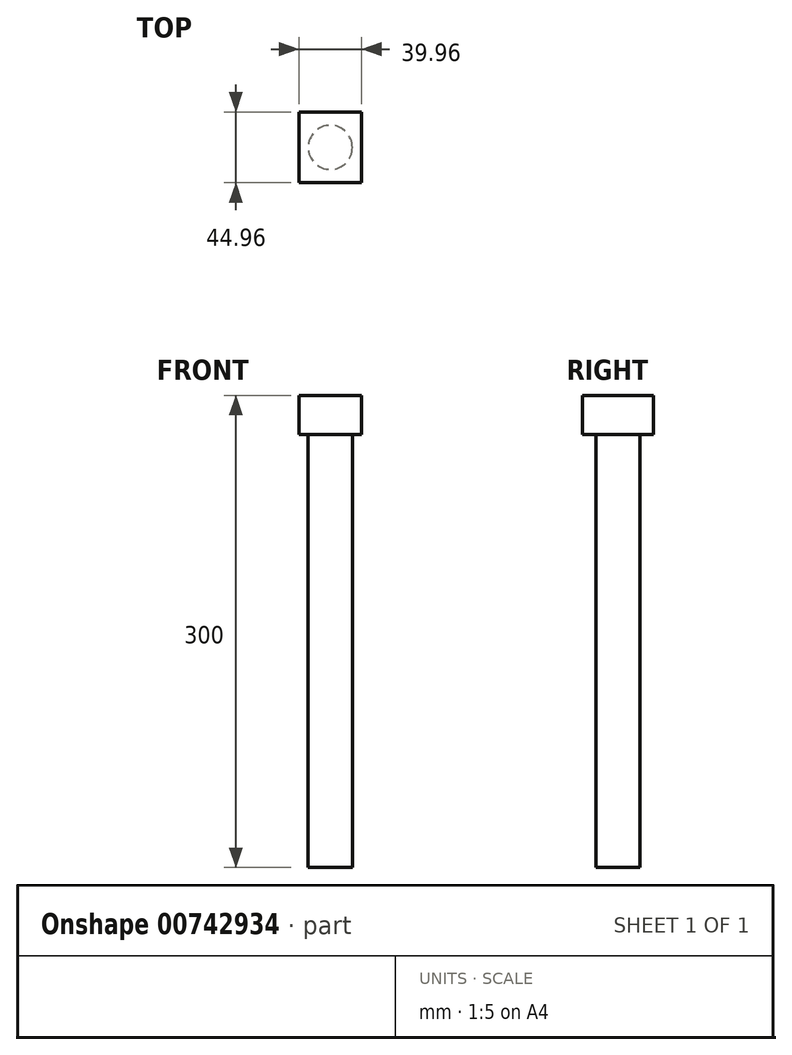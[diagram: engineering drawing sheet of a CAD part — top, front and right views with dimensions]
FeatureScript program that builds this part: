
annotation { "Feature Type Name" : "Feature", "Feature Type Description" : "" }
export const myFeature = defineFeature(function(context is Context, id is Id, definition is map)
    precondition{}
    {
        {
            var Q0;
            Q0=qCreatedBy(makeId("Top.planeOp"),FACE);
            var sketch = newSketch(context, id + "F0", { "sketchPlane" : qUnion([Q0])});
            skCircle(sketch, "E0", {"center": v(0, 0) * mm, "radius": 14 * mm});
            skSolve(sketch);
        }
        {
            var Q0;
            Q0=qSketchRegion(id+"F0",true);
            extrude(context, id + "F1", {"entities" : qUnion([Q0]), "depth" : 300 * mm, "offsetDistance" : 25 * mm});
        }
        {
            var Q0;
            Q0=makeQuery(id+"F1.opExtrude","CAP_FACE",FACE,{"disambiguationData":[OSD([sQuery(id+"F0.wireOp",EDGE,"E0")])],"isStart":false});
            var sketch = newSketch(context, id + "F2", { "sketchPlane" : qUnion([Q0])});
            skLineSegment(sketch, "E1.bottom", {"start": v(19.98, -22.48) * mm, "end": v(-19.98, -22.48) * mm});
            skLineSegment(sketch, "E1.top", {"start": v(19.98, 22.48) * mm, "end": v(-19.98, 22.48) * mm});
            skLineSegment(sketch, "E1.left", {"start": v(19.98, -22.48) * mm, "end": v(19.98, 22.48) * mm});
            skLineSegment(sketch, "E1.right", {"start": v(-19.98, -22.48) * mm, "end": v(-19.98, 22.48) * mm});
            skPoint(sketch, "E1.middle", {"position": v(0, 0) * mm});
            skSolve(sketch);
        }
        {
            var Q0;
            Q0=makeQuery(id+"F2.imprint","IMPRINT",FACE,{"disambiguationData":[TD([[makeQuery(id+"F2.imprint","IMPRINT",EDGE,{"derivedFrom":sQuery(id+"F2.wireOp",EDGE,"E1.bottom")}),-1.0]])]});
            extrude(context, id + "F3", {"entities" : qUnion([Q0]), "operationType" : NewBodyOperationType.ADD, "oppositeDirection" : true, "depth" : 25 * mm, "offsetDistance" : 25 * mm});
        }
    });
